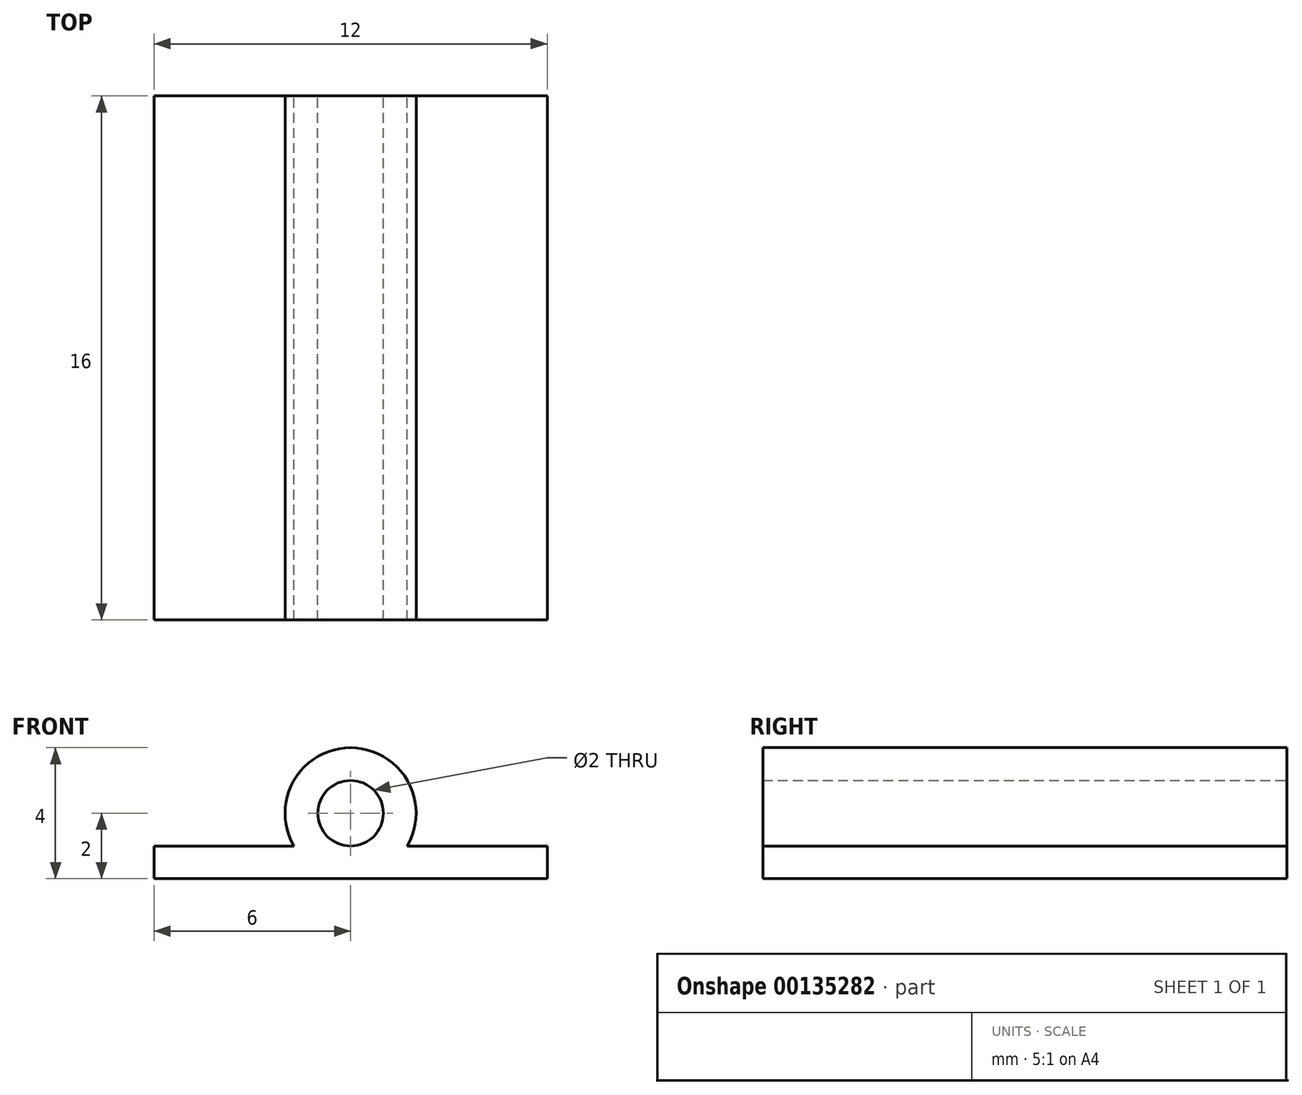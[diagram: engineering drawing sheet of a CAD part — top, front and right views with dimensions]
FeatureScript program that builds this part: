
annotation { "Feature Type Name" : "Feature", "Feature Type Description" : "" }
export const myFeature = defineFeature(function(context is Context, id is Id, definition is map)
    precondition{}
    {
        {
            var Q0;
            Q0=qCreatedBy(makeId("Front.planeOp"),FACE);
            var sketch = newSketch(context, id + "F0", { "sketchPlane" : qUnion([Q0])});
            skLineSegment(sketch, "E0.bottom", {"start": v(0, 0) * mm, "end": v(12, 0) * mm});
            skLineSegment(sketch, "E0.top", {"start": v(0, 1) * mm, "end": v(4.27, 1) * mm});
            skLineSegment(sketch, "E0.left", {"start": v(0, 0) * mm, "end": v(0, 1) * mm});
            skLineSegment(sketch, "E0.right", {"start": v(12, 0) * mm, "end": v(12, 1) * mm});
            skPoint(sketch, "E1.endSnap0", {"position": v(6, 1) * mm});
            skArc(sketch, "E2", {"start": v(7.73, 1) * mm, "mid": v(6, 4) * mm, "end": v(4.27, 1) * mm});
            skCircle(sketch, "E3", {"center": v(6, 2) * mm, "radius": 1 * mm});
            skLineSegment(sketch, "E4.trimOffspring", {"start": v(7.73, 1) * mm, "end": v(12, 1) * mm});
            skSolve(sketch);
        }
        {
            var Q0;
            Q0 = qSketchRegion(id + "F0", true);
            extrude(context, id + "F1", {"entities" : qUnion([Q0]), "depth" : 16 * mm});
        }
    });
